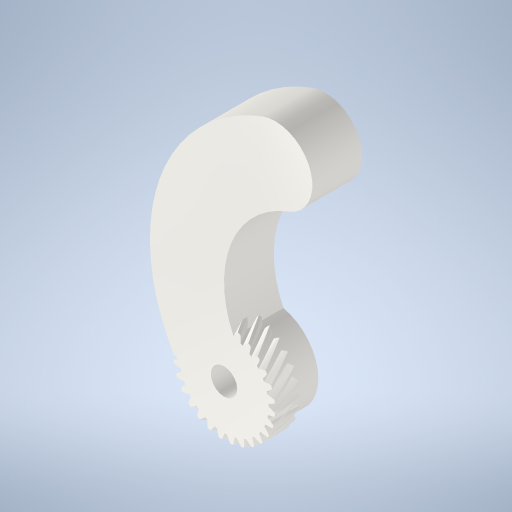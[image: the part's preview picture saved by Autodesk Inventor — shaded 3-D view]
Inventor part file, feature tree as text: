
AUTODESK INVENTOR PART (.ipt)
format: ipt  version: 2024 (Build 280153000, 153)  size: 1,325,056 bytes
history: native  units: mm (DEFAULTED — no unit token found)
features: extrude x3, plane x3, other x3, sketch x3, projected_geometry x1
ambient origin geometry x8: Origin, YZ Plane, XZ Plane, XY Plane, X Axis, Y Axis, Z Axis, Center Point
bodies: Solid1 (feature_tree)
feature tree (13):
  extrude  "Extrusion1"  Depth=5.0mm TaperAngle=0.0deg
  plane  "Work Plane2"
  plane  "Work Plane8"
  plane  "Work Plane9"
  other  "Spur Gear"
  extrude  "Extrusion2"  Depth=10.0mm TaperAngle=0.0deg
  extrude  "Extrusion3"  Depth=10.0mm TaperAngle=0.0deg
  sketch  "Sketch1"  dims[d0=20.587946mm d1=5.0mm d2=0.0mm]
  other  "Srf1"
  sketch  "Sketch3"  dims[d3=19.398969mm d4=10.0mm d5=0.0mm]
  sketch  "Sketch4"  dims[d16=20.0mm d17=0.0mm d34=1.121997mm d39=0.0mm d41=0.0mm d43=20.0mm d46=20.0mm d47=0.0mm d48=0.0mm d49=5.3mm d50=10.0mm d51=0.0mm d52=10.0mm d53=10.0mm d54=40.0mm d55=20.0mm d60=10.0mm d61=0.0mm d62=69.791828mm d63=43.0mm]
  projected_geometry  "Projected Loop1"
  other  "Pitch Diameter"
